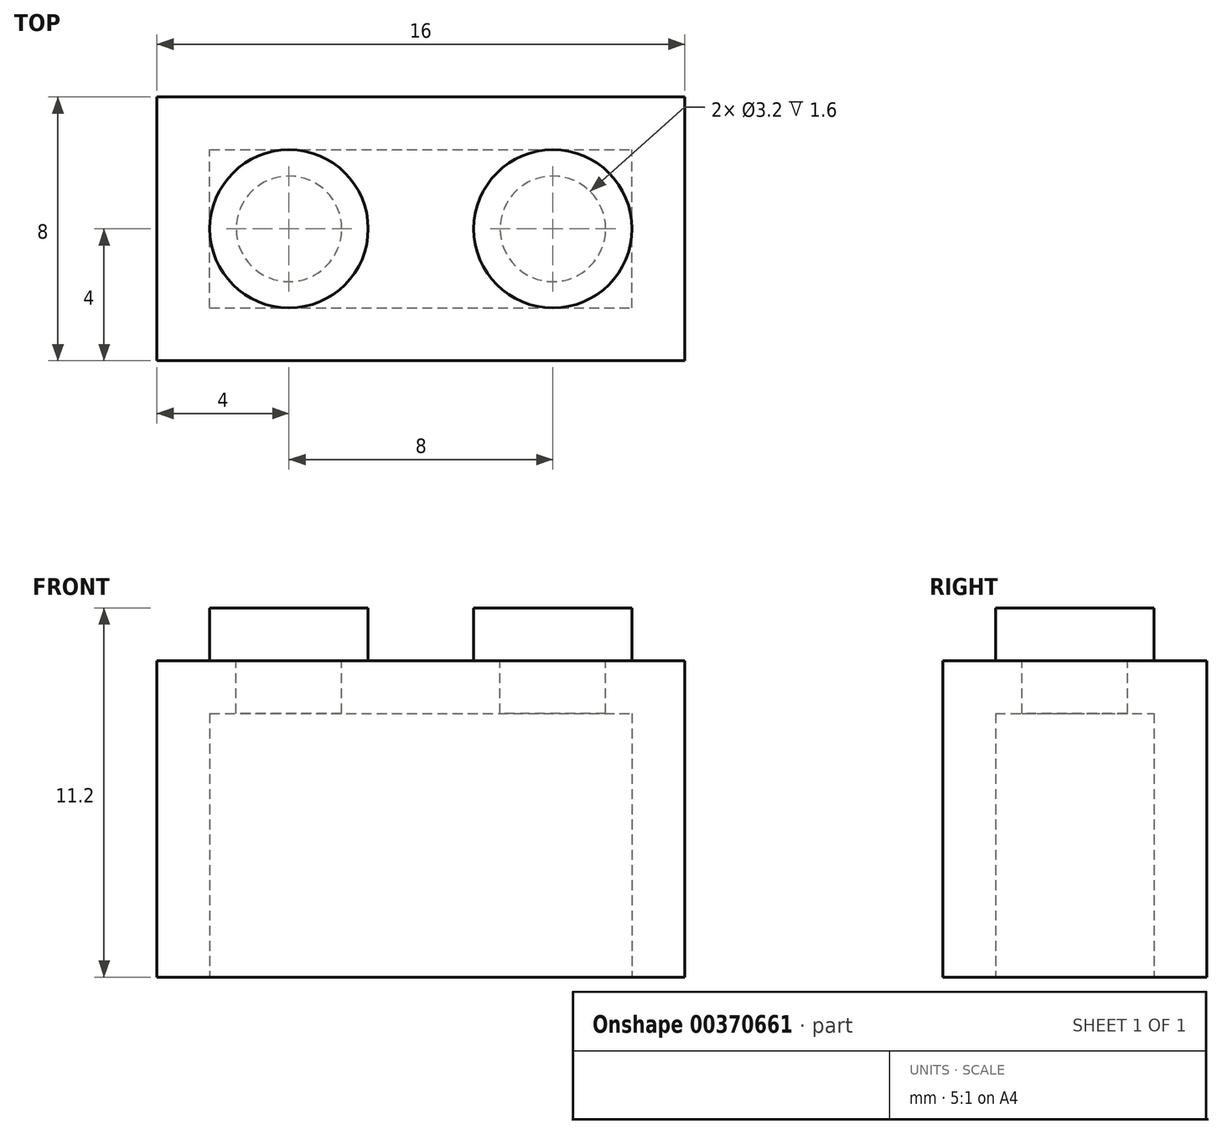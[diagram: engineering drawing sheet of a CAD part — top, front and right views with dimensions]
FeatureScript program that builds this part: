
annotation { "Feature Type Name" : "Feature", "Feature Type Description" : "" }
export const myFeature = defineFeature(function(context is Context, id is Id, definition is map)
    precondition{}
    {
        {
            var Q0;
            Q0=qCreatedBy(makeId("Top.planeOp"),FACE);
            var sketch = newSketch(context, id + "F0", { "sketchPlane" : qUnion([Q0])});
            skLineSegment(sketch, "E0.bottom", {"start": v(-8, -4) * mm, "end": v(8, -4) * mm});
            skLineSegment(sketch, "E0.top", {"start": v(-8, 4) * mm, "end": v(8, 4) * mm});
            skLineSegment(sketch, "E0.left", {"start": v(-8, -4) * mm, "end": v(-8, 4) * mm});
            skLineSegment(sketch, "E0.right", {"start": v(8, -4) * mm, "end": v(8, 4) * mm});
            skPoint(sketch, "E0.middle", {"position": v(0, 0) * mm});
            skLineSegment(sketch, "E1.0", {"start": v(-6.4, -2.4) * mm, "end": v(6.4, -2.4) * mm});
            skLineSegment(sketch, "E1.1", {"start": v(-6.4, -2.4) * mm, "end": v(-6.4, 2.4) * mm});
            skLineSegment(sketch, "E1.2", {"start": v(-6.4, 2.4) * mm, "end": v(6.4, 2.4) * mm});
            skLineSegment(sketch, "E1.3", {"start": v(6.4, -2.4) * mm, "end": v(6.4, 2.4) * mm});
            skSolve(sketch);
        }
        {
            var Q0;
            Q0 = qSketchRegion(id + "F0", true);
            var Q1;
            Q1=makeQuery(id+"F0.imprint","IMPRINT",FACE,{"disambiguationData":[TD([[makeQuery(id+"F0.imprint","IMPRINT",EDGE,{"derivedFrom":sQuery(id+"F0.wireOp",EDGE,"E1.0")}),1.0]])]});
            extrude(context, id + "F1", {"entities" : qUnion([Q0, Q1]), "depth" : 9.6 * mm});
        }
        {
            var Q0;
            Q0=makeQuery(id+"F0.imprint","IMPRINT",FACE,{"disambiguationData":[TD([[makeQuery(id+"F0.imprint","IMPRINT",EDGE,{"derivedFrom":sQuery(id+"F0.wireOp",EDGE,"E1.0")}),1.0]])]});
            extrude(context, id + "F2", {"entities" : qUnion([Q0]), "operationType" : NewBodyOperationType.REMOVE, "depth" : 8 * mm});
        }
        {
            var Q0;
            Q0=makeQuery(id+"F1.opExtrude","CAP_FACE",FACE,{"disambiguationData":[OSD([sQuery(id+"F0.wireOp",EDGE,"E0.bottom"),sQuery(id+"F0.wireOp",EDGE,"E0.top"),sQuery(id+"F0.wireOp",EDGE,"E0.left"),sQuery(id+"F0.wireOp",EDGE,"E0.right")])],"isStart":false});
            var sketch = newSketch(context, id + "F3", { "sketchPlane" : qUnion([Q0])});
            skPoint(sketch, "E2", {"position": v(4, 0) * mm});
            skCircle(sketch, "E3", {"center": v(4, 0) * mm, "radius": 1.6 * mm});
            skCircle(sketch, "E4", {"center": v(-4, 0) * mm, "radius": 1.6 * mm});
            skSolve(sketch);
        }
        {
            var Q0;
            Q0 = qSketchRegion(id + "F3", true);
            extrude(context, id + "F4", {"entities" : qUnion([Q0]), "operationType" : NewBodyOperationType.REMOVE, "oppositeDirection" : true, "depth" : 1.6 * mm});
        }
        {
            var Q0;
            Q0=makeQuery(id+"F1.opExtrude","CAP_FACE",FACE,{"disambiguationData":[OSD([sQuery(id+"F0.wireOp",EDGE,"E0.bottom"),sQuery(id+"F0.wireOp",EDGE,"E0.top"),sQuery(id+"F0.wireOp",EDGE,"E0.left"),sQuery(id+"F0.wireOp",EDGE,"E0.right")])],"isStart":false});
            var sketch = newSketch(context, id + "F5", { "sketchPlane" : qUnion([Q0])});
            skCircle(sketch, "E5", {"center": v(-4, 0) * mm, "radius": 2.4 * mm});
            skCircle(sketch, "E6", {"center": v(4, 0) * mm, "radius": 2.4 * mm});
            skSolve(sketch);
        }
        {
            var Q0;
            Q0 = qSketchRegion(id + "F5", true);
            extrude(context, id + "F6", {"entities" : qUnion([Q0]), "operationType" : NewBodyOperationType.ADD, "depth" : 1.6 * mm});
        }
    });
